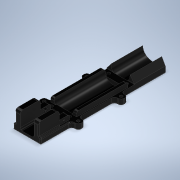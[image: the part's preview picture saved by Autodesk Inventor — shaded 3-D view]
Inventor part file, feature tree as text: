
AUTODESK INVENTOR PART (.ipt)
format: ipt  version: 2020.2 (Build 242310000, 310)  size: 826,368 bytes
history: native  units: mm
features: projected_geometry x25, extrude x18, sketch x18, fillet x9, hole x2, chamfer x2, plane x1, direct_edit x1, move_body x1
ambient origin geometry x8: Origin, YZ Plane, XZ Plane, XY Plane, X Axis, Y Axis, Z Axis, Center Point
bodies: Solid1 (feature_tree)
feature tree (77):
  extrude  "Extrusion1"  Depth=100.0mm
  plane  "Work Plane1"
  sketch  "Sketch2"  dims[d2=6.0mm d3=0.0mm d4=-7.0mm]
  extrude  "Extrusion2"  [1 undecoded]
  extrude  "Extrusion7"  Depth=21.5mm
  extrude  "Extrusion3"  Depth=12.5mm
  hole  "Hole1"  [1 undecoded]
  direct_edit  "Direct Edit1"
  extrude  "Extrusion4"  Depth=5.0mm
  extrude  "Extrusion5"  Depth=5.0mm
  extrude  "Extrusion6"  Depth=5.0mm
  hole  "Hole2"  [1 undecoded]
  extrude  "Extrusion8"  Depth=31.0mm TaperAngle=0.0deg
  fillet  "Fillet1"  Radius=10.5mm
  fillet  "Fillet2"  Radius=31.0mm
  fillet  "Fillet3"  Radius=2.95mm
  chamfer  "Chamfer1"  Distance=14.0mm
  chamfer  "Chamfer2"  Distance=6.0mm
  fillet  "Fillet4"  Radius=3.5mm
  extrude  "Extrusion9"  Depth=3.0mm
  fillet  "Fillet5"  Radius=3.5mm
  extrude  "Extrusion10"  Depth=3.0mm
  extrude  "Extrusion11"  Depth=31.0mm
  extrude  "Extrusion12"  Depth=3.0mm
  extrude  "Extrusion13"  Depth=3.0mm
  fillet  "Fillet6"  Radius=6.75mm
  extrude  "Extrusion14"  Depth=3.0mm
  extrude  "Extrusion15"  Depth=3.0mm
  fillet  "Fillet7"  Radius=152.0mm
  fillet  "Fillet8"  Radius=85.25mm
  extrude  "Extrusion16"  Depth=1.0mm
  fillet  "Fillet9"  Radius=3.0mm
  extrude  "Extrusion17"  Depth=1.0mm
  extrude  "Extrusion18"  Depth=3.0mm TaperAngle=45.0deg
  sketch  "Sketch1"  dims[d0=29.0mm d1=100.0mm]
  projected_geometry  "Projected Loop1"
  sketch  "Sketch3"  dims[d5=12.5mm d6=21.5mm]
  projected_geometry  "Projected Loop2"
  sketch  "Sketch4"  dims[d7=51.8mm d8=0.0mm d9=12.5mm]
  projected_geometry  "Projected Loop3"
  sketch  "Sketch5"  dims[d10=20.0mm d11=34.0mm d12=0.0mm]
  projected_geometry  "Projected Loop4"
  projected_geometry  "Projected Loop5"
  sketch  "Sketch7"  dims[d13=3.0mm d14=5.0mm]
  projected_geometry  "Projected Loop6"
  sketch  "Sketch8"  dims[d15=3.0mm d16=5.0mm]
  projected_geometry  "Projected Loop7"
  sketch  "Sketch9"  dims[d17=3.1mm d18=6.0mm d19=5.5mm d20=2.0mm d21=90.0deg d22=6.0mm d23=0.0mm d24=5.0mm]
  projected_geometry  "Projected Loop8"
  sketch  "Sketch10"  dims[d25=63.0mm d26=5.0mm]
  projected_geometry  "Projected Loop9"
  sketch  "Sketch11"  dims[d27=63.0mm d28=0.0mm d29=0.0mm d30=31.0mm d31=10.5mm d32=31.0mm d33=2.95mm d34=0.0mm]
  projected_geometry  "Projected Loop10"
  sketch  "Sketch12"  dims[d35=5.0mm]
  projected_geometry  "Projected Loop11"
  projected_geometry  "Projected Loop12"
  projected_geometry  "Projected Loop13"
  sketch  "Sketch14"  dims[d36=20.0mm]
  sketch  "Sketch16"  dims[d37=5.0mm]
  projected_geometry  "Projected Loop22"
  sketch  "Sketch17"  dims[d38=20.0mm d39=14.0mm d40=0.0mm]
  projected_geometry  "Projected Loop23"
  projected_geometry  "Projected Loop24"
  projected_geometry  "Projected Loop25"
  sketch  "Sketch18"  dims[d41=7.0mm]
  projected_geometry  "Projected Loop26"
  projected_geometry  "Projected Loop27"
  projected_geometry  "Projected Loop28"
  projected_geometry  "Projected Loop29"
  projected_geometry  "Projected Loop30"
  sketch  "Sketch19"  dims[d42=7.0mm]
  projected_geometry  "Projected Loop31"
  projected_geometry  "Projected Loop32"
  sketch  "Sketch20"  dims[d43=7.0mm]
  projected_geometry  "Projected Loop33"
  sketch  "Sketch21"  dims[d44=7.0mm d45=6.0mm d46=0.0mm d47=3.5mm d48=3.5mm d49=3.5mm d50=3.5mm d51=3.1mm d52=6.0mm d53=5.5mm d54=2.0mm d55=90.0deg d56=6.0mm d57=0.0mm d58=31.0mm d59=38.0mm d60=34.0mm d61=6.75mm d62=0.0mm d63=55.0mm d64=176.0mm d65=152.0mm d66=85.25mm d67=0.0mm d68=1.0mm d69=3.0mm d70=3.0mm d71=3.0mm d72=1.0mm d73=4.5mm d74=6.0mm d75=45.0deg d76=4.5mm d77=6.0mm d78=45.0deg d79=1.0mm d80=1.45mm d81=0.0mm d82=3.0mm d83=1.0mm d84=6.1mm d85=27.2mm d87=14.5mm d88=53.8mm d89=0.1mm d90=0.1mm d91=5.0mm d92=0.0mm d93=5.0mm d94=53.75mm d95=0.0mm d96=0.0mm d98=15.0mm d99=0.0mm d100=17.25mm d101=0.0mm d102=2.0mm d103=0.15mm d104=0.15mm d105=0.15mm d106=0.15mm d107=0.0mm d108=17.25mm d109=0.0mm d110=8.25mm d111=0.0mm d112=2.0mm d113=0.25mm d114=1.0mm d115=0.0mm d116=2.0mm d117=5.0mm d118=2.5mm d119=0.6mm d120=0.75mm d121=9.125mm d122=0.0mm d123=4.0mm d124=17.75mm d125=3.0mm d126=0.0mm d127=0.0mm]
  move_body  "Move1"
note: 3 required parameter values undecoded (feature->parameter linkage not recoverable at this tier; creation-order binding heuristic only, values carry confidence <= 0.55)
